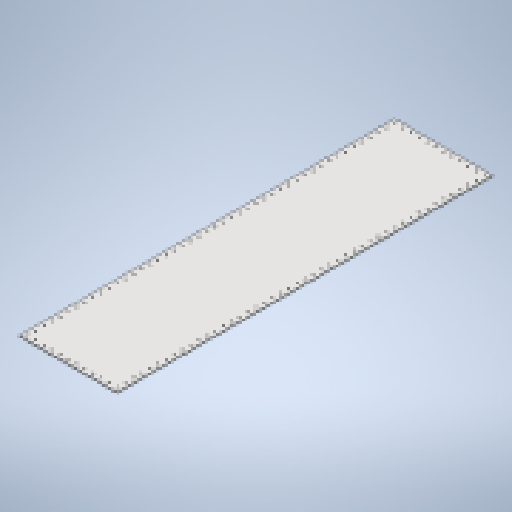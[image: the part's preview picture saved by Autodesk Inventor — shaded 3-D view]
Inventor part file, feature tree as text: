
AUTODESK INVENTOR PART (.ipt)
format: ipt  version: 2023.4 (Build 274418000, 418)  size: 416,768 bytes
history: native  units: in
note: dims shown in document units (in); Inventor stores cm internally (conversion verified against a paired STEP export)
features: sheet_metal_op x1, extrude x1, other x1, sketch x1
ambient origin geometry x8: Origin, YZ Plane, XZ Plane, XY Plane, X Axis, Y Axis, Z Axis, Center Point
bodies: Body1 (feature_tree)
feature tree (4):
  sheet_metal_op  "Face2"
  extrude  "Extrusion6"  Depth=12.0in
  other  "Plate2"
  sketch  "Sketch4"  dims[d0=46.0in d1=12.0in d3=0.197in d4=0.5in d5=0.5in d6=0.197in d7=0.5in d8=0.5in d9=4.7244in d11=1.0in d12=0.3937in d14=1.0in d16=18.1102in d18=1.0in d19=0.3937in d21=1.0in d23=4.7244in d25=1.0in d26=0.3937in d28=1.0in d30=17.7165in d32=1.0in d33=0.3937in d35=1.0in d37=0.125in d83=8.0in d84=11.0in d85=2.0in d86=2.0in d87=1.5in d88=1.0in d89=0.0in d49=0.5in d50=0.0344in d51=0.5in d52=0.0344in]
